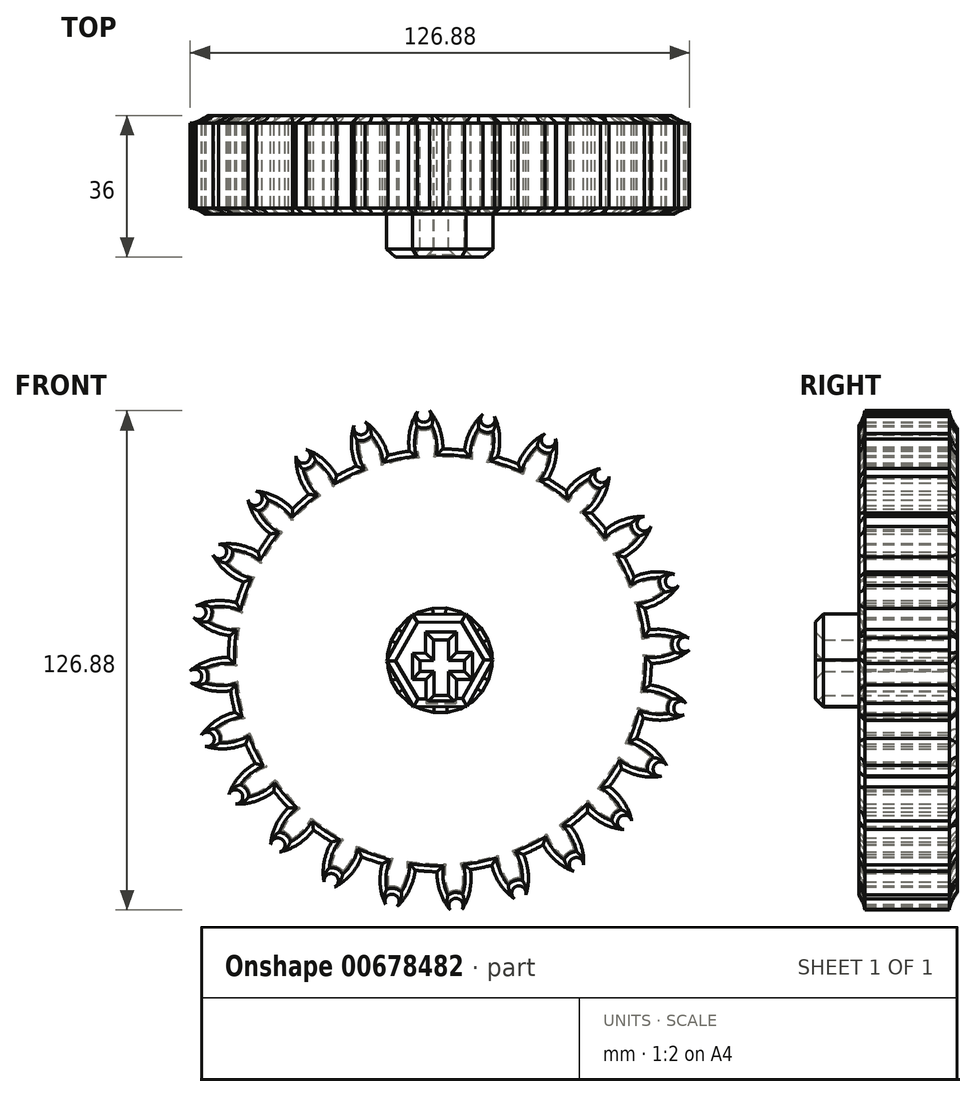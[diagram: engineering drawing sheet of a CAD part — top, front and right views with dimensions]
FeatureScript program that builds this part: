
annotation { "Feature Type Name" : "Feature", "Feature Type Description" : "" }
export const myFeature = defineFeature(function(context is Context, id is Id, definition is map)
    precondition{}
    {
        {
            var Q0;
            Q0=qCreatedBy(makeId("Front.planeOp"),FACE);
            var sketch = newSketch(context, id + "F0", { "sketchPlane" : qUnion([Q0])});
            skCircle(sketch, "E0", {"center": v(0, 0) * mm, "radius": 58.67 * mm, "construction": true});
            skCircle(sketch, "E1", {"center": v(0, 0) * mm, "radius": 53.72 * mm});
            skCircle(sketch, "E2", {"center": v(0, 0) * mm, "radius": 63.5 * mm, "construction": true});
            skLineSegment(sketch, "E3", {"start": v(0, 0) * mm, "end": v(0, 86.23) * mm, "construction": true});
            skLineSegment(sketch, "E4", {"start": v(0, 0) * mm, "end": v(-6, 91.64) * mm, "construction": true});
            skLineSegment(sketch, "E5", {"start": v(0, 58.67) * mm, "end": v(-65.6, 60.5) * mm, "construction": true});
            skLineSegment(sketch, "E6", {"start": v(0, 58.67) * mm, "end": v(-64.31, 37.28) * mm, "construction": true});
            skCircle(sketch, "E7", {"center": v(0, 0) * mm, "radius": 55.67 * mm, "construction": true});
            skCircle(sketch, "E8", {"center": v(0, 58.67) * mm, "radius": 14.6 * mm, "construction": true});
            skCircle(sketch, "E9", {"center": v(-13.86, 54.06) * mm, "radius": 14.6 * mm, "construction": true});
            skArc(sketch, "E10", {"start": v(0, 58.67) * mm, "mid": v(-1.1, 61.19) * mm, "end": v(-2.66, 63.44) * mm});
            skArc(sketch, "E11", {"start": v(0.74, 53.72) * mm, "mid": v(0.58, 56.23) * mm, "end": v(0, 58.67) * mm});
            skArc(sketch, "E12.MirrorCS", {"start": v(-7.66, 58.17) * mm, "mid": v(-6.9, 60.8) * mm, "end": v(-5.64, 63.25) * mm});
            skArc(sketch, "E13.MirrorCS", {"start": v(-7.75, 53.16) * mm, "mid": v(-7.91, 55.67) * mm, "end": v(-7.66, 58.17) * mm});
            skArc(sketch, "E14", {"start": v(-5.64, 63.25) * mm, "mid": v(-3.96, 60.49) * mm, "end": v(-2.66, 63.44) * mm});
            skCircle(sketch, "E15", {"center": v(0, 0) * mm, "radius": 37.66 * mm});
            skCircle(sketch, "E16.cCircle", {"center": v(0, 0) * mm, "radius": 13.56 * mm, "construction": true});
            skLineSegment(sketch, "E16.0", {"start": v(6.65, 11.81) * mm, "end": v(13.56, 0.15) * mm});
            skLineSegment(sketch, "E16.1", {"start": v(13.56, 0.15) * mm, "end": v(6.9, -11.66) * mm});
            skLineSegment(sketch, "E16.2", {"start": v(6.9, -11.66) * mm, "end": v(-6.65, -11.81) * mm});
            skLineSegment(sketch, "E16.3", {"start": v(-6.65, -11.81) * mm, "end": v(-13.56, -0.15) * mm});
            skLineSegment(sketch, "E16.4", {"start": v(-13.56, -0.15) * mm, "end": v(-6.9, 11.66) * mm});
            skLineSegment(sketch, "E16.5", {"start": v(-6.9, 11.66) * mm, "end": v(6.65, 11.81) * mm});
            skLineSegment(sketch, "E17", {"start": v(-1.68, 5.23) * mm, "end": v(2.17, 5.23) * mm});
            skLineSegment(sketch, "E18", {"start": v(2.17, 5.23) * mm, "end": v(2.17, 0) * mm});
            skLineSegment(sketch, "E19", {"start": v(-1.68, 5.23) * mm, "end": v(-1.68, 0) * mm});
            skLineSegment(sketch, "E20", {"start": v(2.17, 0) * mm, "end": v(6.24, 0) * mm});
            skLineSegment(sketch, "E21", {"start": v(6.24, 0) * mm, "end": v(6.24, -2.8) * mm});
            skLineSegment(sketch, "E22", {"start": v(6.24, -2.8) * mm, "end": v(2.17, -2.8) * mm});
            skLineSegment(sketch, "E23", {"start": v(2.17, -2.8) * mm, "end": v(2.17, -8.9) * mm});
            skLineSegment(sketch, "E24", {"start": v(2.17, -8.9) * mm, "end": v(-1.47, -8.9) * mm});
            skLineSegment(sketch, "E25", {"start": v(-1.47, -8.9) * mm, "end": v(-1.47, -2.8) * mm});
            skLineSegment(sketch, "E26", {"start": v(-1.47, -2.8) * mm, "end": v(-5, -2.8) * mm});
            skLineSegment(sketch, "E27", {"start": v(-5, -2.8) * mm, "end": v(-5, 0) * mm});
            skLineSegment(sketch, "E28", {"start": v(-5, -0.13) * mm, "end": v(-1.68, 0) * mm});
            skSolve(sketch);
        }
        {
            var Q0;
            {var subQ0=sQuery(id+"F0.wireOp",EDGE,"E1");var subQ1=makeQuery(id+"F0.imprint","INTERSECT",VERTEX,{"derivedFrom":[subQ0,sQuery(id+"F0.wireOp",EDGE,"E11")]});Q0=makeQuery(id+"F0.imprint","IMPRINT",FACE,{"disambiguationData":[TD([[makeQuery(id+"F0.imprint","IMPRINT",EDGE,{"disambiguationData":[TD([[subQ1,-1.0]])],"derivedFrom":subQ0}),1.0]])]});}
            var Q1;
            Q1=makeQuery(id+"F0.imprint","IMPRINT",FACE,{"disambiguationData":[TD([[makeQuery(id+"F0.imprint","IMPRINT",EDGE,{"derivedFrom":sQuery(id+"F0.wireOp",EDGE,"E10")}),1.0]])]});
            var Q2;
            Q2=makeQuery(id+"F0.imprint","IMPRINT",FACE,{"disambiguationData":[TD([[makeQuery(id+"F0.imprint","IMPRINT",EDGE,{"derivedFrom":sQuery(id+"F0.wireOp",EDGE,"E15")}),1.0]])]});
            extrude(context, id + "F1", {"entities" : qUnion([Q0, Q1, Q2]), "depth" : 25 * mm, "offsetDistance" : 25 * mm});
        }
        {
            var Q0;
            Q0=makeQuery(id+"F1.opExtrude","CAP_FACE",FACE,{"disambiguationData":[OSD([sQuery(id+"F0.wireOp",EDGE,"E1"),sQuery(id+"F0.wireOp",EDGE,"E10"),sQuery(id+"F0.wireOp",EDGE,"E11"),sQuery(id+"F0.wireOp",EDGE,"E12.MirrorCS"),sQuery(id+"F0.wireOp",EDGE,"E13.MirrorCS"),sQuery(id+"F0.wireOp",EDGE,"E14"),sQuery(id+"F0.wireOp",EDGE,"mVWzd8jA-rzYP-dDsJ-KGQD-ebWhzy7b6Ves"),sQuery(id+"F0.wireOp",EDGE,"IrgexYyV-O8Q5-9xSA-GD7V-AP3d3zi0KR9e"),sQuery(id+"F0.wireOp",EDGE,"ylAEuyQL-J7rp-u944-eGz3-I0GYt71x9tKg"),sQuery(id+"F0.wireOp",EDGE,"AUASGWqe-mEDw-TZVE-bKdS-i5HWq42x1RMj")])],"isStart":false});
            chamfer(context, id + "F2", {"entities" : qUnion([Q0]), "width" : 1.5 * mm, "tangentPropagation" : true});
        }
        {
            var Q0;
            Q0=makeQuery(id+"F1.opExtrude","SWEPT_BODY",BODY,{"disambiguationData":[OSD([sQuery(id+"F0.wireOp",EDGE,"E1"),sQuery(id+"F0.wireOp",EDGE,"E10"),sQuery(id+"F0.wireOp",EDGE,"E11"),sQuery(id+"F0.wireOp",EDGE,"E12.MirrorCS"),sQuery(id+"F0.wireOp",EDGE,"E13.MirrorCS"),sQuery(id+"F0.wireOp",EDGE,"E14")])]});
            var Q1;
            Q1=makeQuery(id+"F1.opExtrude","SWEPT_FACE",FACE,{"disambiguationData":[OSD([sQuery(id+"F0.wireOp",EDGE,"E1")])]});
            circularPattern(context, id + "F3", {"entities" : qUnion([Q0]), "axis" : qUnion([Q1]), "angle" : 360 * degree, "instanceCount" : 24, "equalSpace" : true});
        }
        {
            var Q0;
            Q0=makeQuery(id+"F0.imprint","IMPRINT",FACE,{"disambiguationData":[TD([[makeQuery(id+"F0.imprint","IMPRINT",EDGE,{"derivedFrom":sQuery(id+"F0.wireOp",EDGE,"E16.0")}),-1.0]])]});
            extrude(context, id + "F4", {"entities" : qUnion([Q0]), "operationType" : NewBodyOperationType.ADD, "depth" : 36 * mm, "offsetDistance" : 25 * mm});
        }
        {
            var Q0;
            Q0=makeQuery(id+"F4.opExtrude","CAP_FACE",FACE,{"disambiguationData":[OSD([sQuery(id+"F0.wireOp",EDGE,"E16.0"),sQuery(id+"F0.wireOp",EDGE,"E16.1"),sQuery(id+"F0.wireOp",EDGE,"E16.2"),sQuery(id+"F0.wireOp",EDGE,"E16.3"),sQuery(id+"F0.wireOp",EDGE,"E16.4"),sQuery(id+"F0.wireOp",EDGE,"E16.5"),sQuery(id+"F0.wireOp",EDGE,"E17"),sQuery(id+"F0.wireOp",EDGE,"E18"),sQuery(id+"F0.wireOp",EDGE,"E19"),sQuery(id+"F0.wireOp",EDGE,"E20"),sQuery(id+"F0.wireOp",EDGE,"E21"),sQuery(id+"F0.wireOp",EDGE,"E22"),sQuery(id+"F0.wireOp",EDGE,"E23"),sQuery(id+"F0.wireOp",EDGE,"E24"),sQuery(id+"F0.wireOp",EDGE,"E25"),sQuery(id+"F0.wireOp",EDGE,"E26"),sQuery(id+"F0.wireOp",EDGE,"E27"),sQuery(id+"F0.wireOp",EDGE,"E28")])],"isStart":false});
            var Q1;
            {var subQ0=sQuery(id+"F0.wireOp",EDGE,"E16.5");var subQ1=sQuery(id+"F0.wireOp",EDGE,"E16.4");var subQ2=sQuery(id+"F0.wireOp",EDGE,"E16.3");var subQ3=sQuery(id+"F0.wireOp",EDGE,"E16.2");var subQ4=sQuery(id+"F0.wireOp",EDGE,"E16.1");var subQ5=sQuery(id+"F0.wireOp",EDGE,"E16.0");var subQ6=makeQuery(id+"F1.opExtrude","CAP_FACE",FACE,{"disambiguationData":[OSD([sQuery(id+"F0.wireOp",EDGE,"E1"),sQuery(id+"F0.wireOp",EDGE,"E10"),sQuery(id+"F0.wireOp",EDGE,"E11"),sQuery(id+"F0.wireOp",EDGE,"E12.MirrorCS"),sQuery(id+"F0.wireOp",EDGE,"E13.MirrorCS"),sQuery(id+"F0.wireOp",EDGE,"E14"),subQ5,subQ4,subQ3,subQ2,subQ1,subQ0])],"isStart":true});Q1=makeQuery(id+"F4.boolean.opBoolean","MERGE",FACE,{"derivedFrom":[subQ6,makeQuery(id+"F3.opPattern","COPY",FACE,{"derivedFrom":subQ6,"instanceName":"1"}),makeQuery(id+"F3.opPattern","COPY",FACE,{"derivedFrom":subQ6,"instanceName":"2"}),makeQuery(id+"F3.opPattern","COPY",FACE,{"derivedFrom":subQ6,"instanceName":"3"}),makeQuery(id+"F3.opPattern","COPY",FACE,{"derivedFrom":subQ6,"instanceName":"4"}),makeQuery(id+"F3.opPattern","COPY",FACE,{"derivedFrom":subQ6,"instanceName":"5"}),makeQuery(id+"F3.opPattern","COPY",FACE,{"derivedFrom":subQ6,"instanceName":"6"}),makeQuery(id+"F3.opPattern","COPY",FACE,{"derivedFrom":subQ6,"instanceName":"7"}),makeQuery(id+"F3.opPattern","COPY",FACE,{"derivedFrom":subQ6,"instanceName":"8"}),makeQuery(id+"F3.opPattern","COPY",FACE,{"derivedFrom":subQ6,"instanceName":"9"}),makeQuery(id+"F3.opPattern","COPY",FACE,{"derivedFrom":subQ6,"instanceName":"10"}),makeQuery(id+"F3.opPattern","COPY",FACE,{"derivedFrom":subQ6,"instanceName":"11"}),makeQuery(id+"F3.opPattern","COPY",FACE,{"derivedFrom":subQ6,"instanceName":"12"}),makeQuery(id+"F3.opPattern","COPY",FACE,{"derivedFrom":subQ6,"instanceName":"13"}),makeQuery(id+"F3.opPattern","COPY",FACE,{"derivedFrom":subQ6,"instanceName":"14"}),makeQuery(id+"F3.opPattern","COPY",FACE,{"derivedFrom":subQ6,"instanceName":"15"}),makeQuery(id+"F3.opPattern","COPY",FACE,{"derivedFrom":subQ6,"instanceName":"16"}),makeQuery(id+"F3.opPattern","COPY",FACE,{"derivedFrom":subQ6,"instanceName":"17"}),makeQuery(id+"F3.opPattern","COPY",FACE,{"derivedFrom":subQ6,"instanceName":"18"}),makeQuery(id+"F3.opPattern","COPY",FACE,{"derivedFrom":subQ6,"instanceName":"19"}),makeQuery(id+"F3.opPattern","COPY",FACE,{"derivedFrom":subQ6,"instanceName":"20"}),makeQuery(id+"F3.opPattern","COPY",FACE,{"derivedFrom":subQ6,"instanceName":"21"}),makeQuery(id+"F3.opPattern","COPY",FACE,{"derivedFrom":subQ6,"instanceName":"22"}),makeQuery(id+"F3.opPattern","COPY",FACE,{"derivedFrom":subQ6,"instanceName":"23"}),makeQuery(id+"F4.opExtrude","CAP_FACE",FACE,{"disambiguationData":[OSD([subQ5,subQ4,subQ3,subQ2,subQ1,subQ0,sQuery(id+"F0.wireOp",EDGE,"E17"),sQuery(id+"F0.wireOp",EDGE,"E18"),sQuery(id+"F0.wireOp",EDGE,"E19"),sQuery(id+"F0.wireOp",EDGE,"E20"),sQuery(id+"F0.wireOp",EDGE,"E21"),sQuery(id+"F0.wireOp",EDGE,"E22"),sQuery(id+"F0.wireOp",EDGE,"E23"),sQuery(id+"F0.wireOp",EDGE,"E24"),sQuery(id+"F0.wireOp",EDGE,"E25"),sQuery(id+"F0.wireOp",EDGE,"E26"),sQuery(id+"F0.wireOp",EDGE,"E27"),sQuery(id+"F0.wireOp",EDGE,"E28")])],"isStart":true})]});}
            chamfer(context, id + "F5", {"entities" : qUnion([Q0, Q1]), "width" : 2 * mm, "tangentPropagation" : true});
        }
    });
